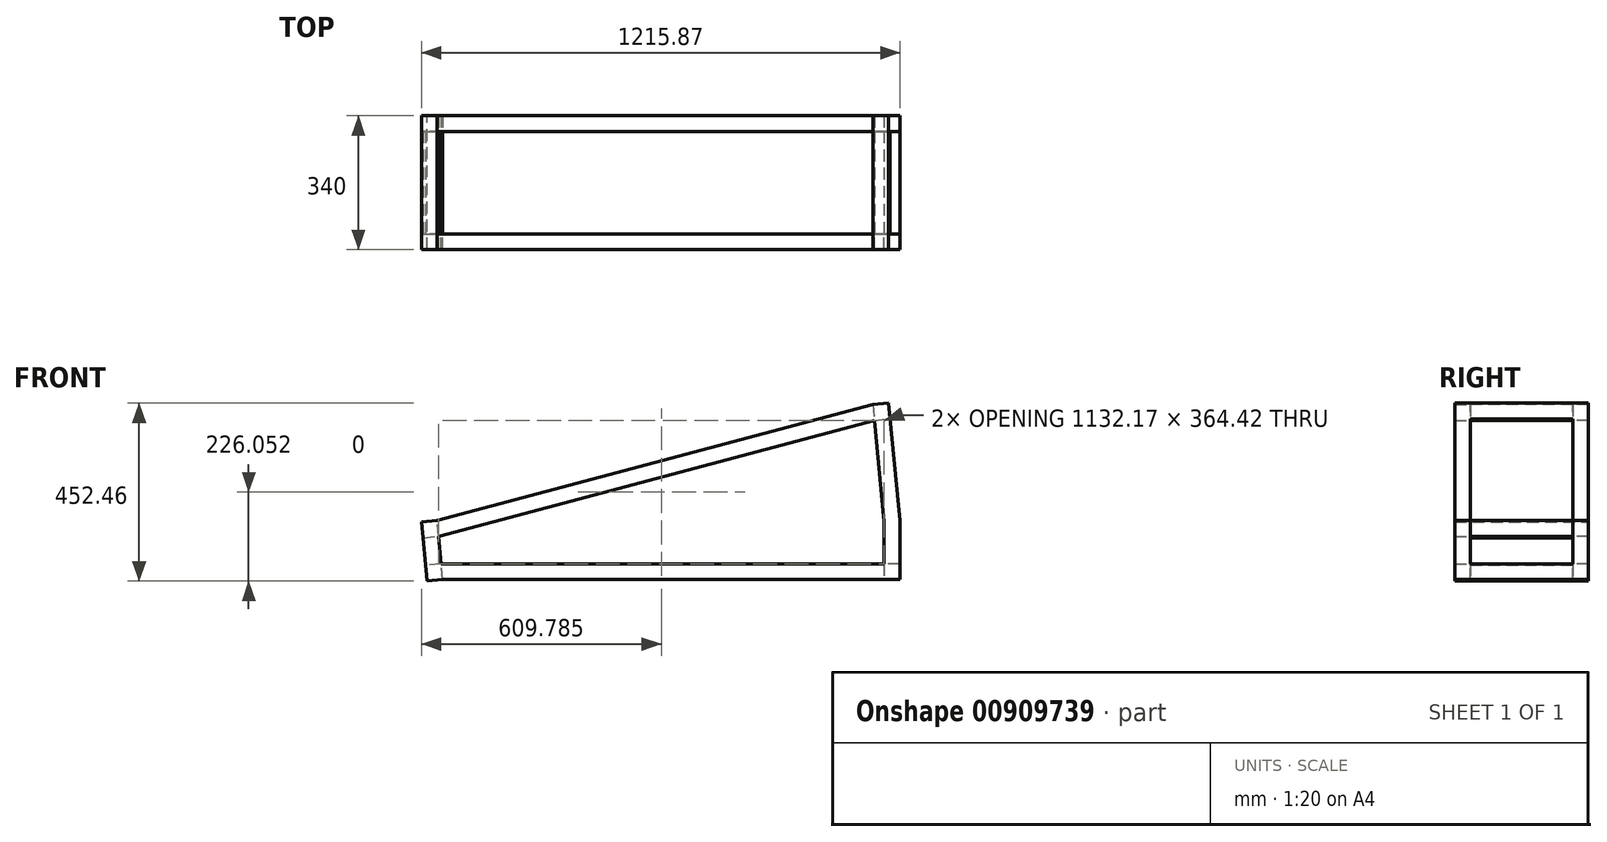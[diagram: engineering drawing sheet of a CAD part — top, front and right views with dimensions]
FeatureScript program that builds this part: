
annotation { "Feature Type Name" : "Feature", "Feature Type Description" : "" }
export const myFeature = defineFeature(function(context is Context, id is Id, definition is map)
    precondition{}
    {
        {
            var Q0;
            Q0=qCreatedBy(makeId("Front.planeOp"),FACE);
            var sketch = newSketch(context, id + "F0", { "sketchPlane" : qUnion([Q0])});
            skLineSegment(sketch, "E0", {"start": v(-1201.42, -3.84) * mm, "end": v(-1215.87, 146.16) * mm});
            skLineSegment(sketch, "E1", {"start": v(-28.76, 448.62) * mm, "end": v(0, 150) * mm});
            skLineSegment(sketch, "E2", {"start": v(0, 150) * mm, "end": v(0, 0) * mm});
            skLineSegment(sketch, "E3", {"start": v(-64.7, 404.42) * mm, "end": v(-40, 148.08) * mm});
            skLineSegment(sketch, "E4", {"start": v(-40, 148.08) * mm, "end": v(-40, 40) * mm});
            skLineSegment(sketch, "E5", {"start": v(-40, 40) * mm, "end": v(-1165.46, 40) * mm});
            skLineSegment(sketch, "E6", {"start": v(-1165.46, 40) * mm, "end": v(-1172.17, 109.64) * mm});
            skLineSegment(sketch, "E7", {"start": v(-1172.17, 109.64) * mm, "end": v(-64.7, 404.42) * mm});
            skLineSegment(sketch, "E8", {"start": v(-28.76, 448.62) * mm, "end": v(-68.58, 444.78) * mm});
            skLineSegment(sketch, "E9", {"start": v(-1215.87, 146.16) * mm, "end": v(-1176.06, 150) * mm});
            skLineSegment(sketch, "E10", {"start": v(-1176.06, 150) * mm, "end": v(-68.58, 444.78) * mm});
            skLineSegment(sketch, "E11", {"start": v(-1201.42, -3.84) * mm, "end": v(-1161.6, 0) * mm});
            skLineSegment(sketch, "E12", {"start": v(-1161.6, 0) * mm, "end": v(0, 0) * mm});
            skPoint(sketch, "E13", {"position": v(-1168.82, 74.82) * mm});
            skPoint(sketch, "E14", {"position": v(-14.38, 299.3) * mm});
            skLineSegment(sketch, "E15", {"start": v(-1168.82, 74.82) * mm, "end": v(-14.38, 299.3) * mm, "construction": true});
            skLineSegment(sketch, "E16", {"start": v(-14.38, 299.3) * mm, "end": v(-1286.3, 299.3) * mm, "construction": true});
            skLineSegment(sketch, "E17", {"start": v(-1168.82, 74.82) * mm, "end": v(314.6, 74.82) * mm, "construction": true});
            skLineSegment(sketch, "E18", {"start": v(-14.38, 299.3) * mm, "end": v(-1474.05, 158.7) * mm, "construction": true});
            skLineSegment(sketch, "E19", {"start": v(-1168.82, 74.82) * mm, "end": v(141.74, 201.06) * mm, "construction": true});
            skSolve(sketch);
        }
        {
            var Q0;
            Q0=makeQuery(id+"F0.imprint","IMPRINT",FACE,{"disambiguationData":[TD([[makeQuery(id+"F0.imprint","IMPRINT",EDGE,{"derivedFrom":sQuery(id+"F0.wireOp",EDGE,"E0")}),-1.0]])]});
            extrude(context, id + "F1", {"entities" : qUnion([Q0]), "depth" : 40 * mm, "offsetDistance" : 25.4 * mm});
        }
        {
            var Q0;
            Q0=makeQuery(id+"F0.imprint","IMPRINT",FACE,{"disambiguationData":[TD([[makeQuery(id+"F0.imprint","IMPRINT",EDGE,{"derivedFrom":sQuery(id+"F0.wireOp",EDGE,"E0")}),-1.0]])]});
            var sketch = newSketch(context, id + "F2", { "sketchPlane" : qUnion([Q0])});
            skSolve(sketch);
        }
        {
            var Q0;
            Q0=makeQuery(id+"F2.imprint","IMPRINT",FACE,{"disambiguationData":[TD([[makeQuery(id+"F2.imprint","IMPRINT",EDGE,{"derivedFrom":makeQuery(id+"F0.imprint","IMPRINT",EDGE,{"derivedFrom":sQuery(id+"F0.wireOp",EDGE,"E0")})}),-1.0]])]});
            var sketch = newSketch(context, id + "F3", { "sketchPlane" : qUnion([Q0])});
            skLineSegment(sketch, "E20", {"start": v(-28.76, 448.62) * mm, "end": v(-68.58, 444.78) * mm});
            skLineSegment(sketch, "E21", {"start": v(-68.58, 444.78) * mm, "end": v(-64.75, 404.97) * mm});
            skLineSegment(sketch, "E22", {"start": v(-64.75, 404.97) * mm, "end": v(-24.93, 408.8) * mm});
            skLineSegment(sketch, "E23", {"start": v(-24.93, 408.8) * mm, "end": v(-28.76, 448.62) * mm});
            skLineSegment(sketch, "E24", {"start": v(0, 40) * mm, "end": v(-40, 40) * mm});
            skLineSegment(sketch, "E25", {"start": v(-40, 40) * mm, "end": v(-40, 0) * mm});
            skLineSegment(sketch, "E26", {"start": v(-40, 0) * mm, "end": v(0, 0) * mm});
            skLineSegment(sketch, "E27", {"start": v(0, 0) * mm, "end": v(0, 40) * mm});
            skLineSegment(sketch, "E28", {"start": v(-1176.06, 150) * mm, "end": v(-1215.87, 146.16) * mm});
            skLineSegment(sketch, "E29", {"start": v(-1215.87, 146.16) * mm, "end": v(-1212.04, 106.35) * mm});
            skLineSegment(sketch, "E30", {"start": v(-1212.04, 106.35) * mm, "end": v(-1172.22, 110.18) * mm});
            skLineSegment(sketch, "E31", {"start": v(-1172.22, 110.18) * mm, "end": v(-1176.06, 150) * mm});
            skLineSegment(sketch, "E32", {"start": v(-1165.44, 39.82) * mm, "end": v(-1205.26, 35.98) * mm});
            skLineSegment(sketch, "E33", {"start": v(-1205.26, 35.98) * mm, "end": v(-1201.42, -3.84) * mm});
            skLineSegment(sketch, "E34", {"start": v(-1201.42, -3.84) * mm, "end": v(-1161.6, 0) * mm});
            skLineSegment(sketch, "E35", {"start": v(-1161.6, 0) * mm, "end": v(-1165.44, 39.82) * mm});
            skSolve(sketch);
        }
        {
            var Q0;
            Q0 = qSketchRegion(id + "F3", true);
            extrude(context, id + "F4", {"entities" : qUnion([Q0]), "operationType" : NewBodyOperationType.ADD, "oppositeDirection" : true, "depth" : 130 * mm, "offsetDistance" : 25 * mm});
        }
        {
            var Q0;
            Q0=makeQuery(id+"F1.opExtrude","SWEPT_BODY",BODY,{"disambiguationData":[OSD([sQuery(id+"F0.wireOp",EDGE,"E0"),sQuery(id+"F0.wireOp",EDGE,"E1"),sQuery(id+"F0.wireOp",EDGE,"E2"),sQuery(id+"F0.wireOp",EDGE,"E3"),sQuery(id+"F0.wireOp",EDGE,"E4"),sQuery(id+"F0.wireOp",EDGE,"E5"),sQuery(id+"F0.wireOp",EDGE,"E6"),sQuery(id+"F0.wireOp",EDGE,"E7"),sQuery(id+"F0.wireOp",EDGE,"E8"),sQuery(id+"F0.wireOp",EDGE,"E9"),sQuery(id+"F0.wireOp",EDGE,"E10"),sQuery(id+"F0.wireOp",EDGE,"E11"),sQuery(id+"F0.wireOp",EDGE,"E12")])]});
            var Q1;
            Q1=makeQuery(id+"F4.opExtrude","CAP_FACE",FACE,{"disambiguationData":[OSD([sQuery(id+"F3.wireOp",EDGE,"E20"),sQuery(id+"F3.wireOp",EDGE,"E21"),sQuery(id+"F3.wireOp",EDGE,"E22"),sQuery(id+"F3.wireOp",EDGE,"E23")])],"isStart":false});
            mirror(context, id + "F5", {"operationType" : NewBodyOperationType.ADD, "entities" : qUnion([Q0]), "mirrorPlane" : qUnion([Q1])});
        }
    });
